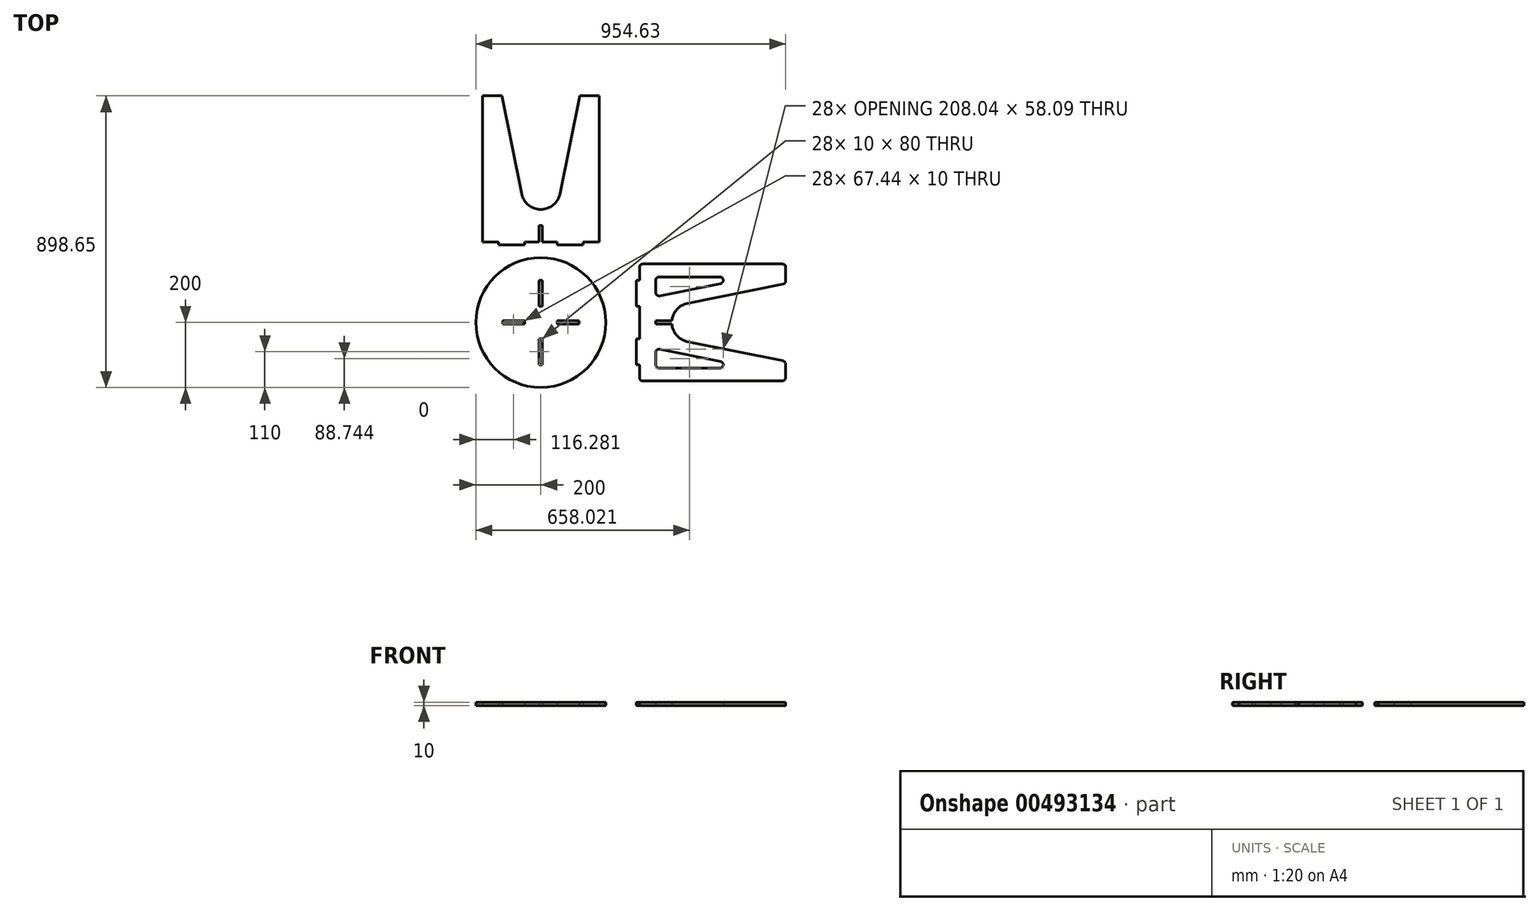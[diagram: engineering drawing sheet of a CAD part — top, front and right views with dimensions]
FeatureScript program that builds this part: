
annotation { "Feature Type Name" : "Feature", "Feature Type Description" : "" }
export const myFeature = defineFeature(function(context is Context, id is Id, definition is map)
    precondition{}
    {
        {
            var Q0;
            Q0=qCreatedBy(makeId("Top.planeOp"),FACE);
            var sketch = newSketch(context, id + "F0", { "sketchPlane" : qUnion([Q0])});
            skCircle(sketch, "E0", {"center": v(0, 0) * mm, "radius": 200 * mm});
            skLineSegment(sketch, "E1.bottom", {"start": v(-5, 130) * mm, "end": v(5, 130) * mm});
            skLineSegment(sketch, "E1.top", {"start": v(-5, 50) * mm, "end": v(5, 50) * mm});
            skLineSegment(sketch, "E1.left", {"start": v(-5, 130) * mm, "end": v(-5, 50) * mm});
            skLineSegment(sketch, "E1.right", {"start": v(5, 130) * mm, "end": v(5, 50) * mm});
            skLineSegment(sketch, "E2.MirrorCS", {"start": v(-5, -50) * mm, "end": v(5, -50) * mm});
            skLineSegment(sketch, "E3.MirrorCS", {"start": v(-5, -130) * mm, "end": v(5, -130) * mm});
            skLineSegment(sketch, "E4.MirrorCS", {"start": v(5, -130) * mm, "end": v(5, -50) * mm});
            skLineSegment(sketch, "E5.MirrorCS", {"start": v(-5, -130) * mm, "end": v(-5, -50) * mm});
            skLineSegment(sketch, "E6.MirrorCS", {"start": v(-117.44, -5) * mm, "end": v(-117.44, 5) * mm});
            skLineSegment(sketch, "E7.MirrorCS", {"start": v(-50, -5) * mm, "end": v(-50, 5) * mm});
            skLineSegment(sketch, "E8.MirrorCS", {"start": v(-50, 5) * mm, "end": v(-117.44, 5) * mm});
            skLineSegment(sketch, "E9.MirrorCS", {"start": v(-50, -5) * mm, "end": v(-117.44, -5) * mm});
            skLineSegment(sketch, "E10.MirrorCS", {"start": v(117.44, -5) * mm, "end": v(117.44, 5) * mm});
            skLineSegment(sketch, "E11.MirrorCS", {"start": v(50, 5) * mm, "end": v(117.44, 5) * mm});
            skLineSegment(sketch, "E12.MirrorCS", {"start": v(50, -5) * mm, "end": v(117.44, -5) * mm});
            skLineSegment(sketch, "E13.MirrorCS", {"start": v(50, -5) * mm, "end": v(50, 5) * mm});
            skLineSegment(sketch, "E14", {"start": v(-180, 248.65) * mm, "end": v(-130, 248.65) * mm});
            skLineSegment(sketch, "E15", {"start": v(180, 248.65) * mm, "end": v(180, 698.65) * mm});
            skLineSegment(sketch, "E16", {"start": v(180, 698.65) * mm, "end": v(120, 698.65) * mm});
            skLineSegment(sketch, "E17", {"start": v(120, 698.65) * mm, "end": v(58.8, 396.73) * mm});
            skLineSegment(sketch, "E18", {"start": v(130, 248.65) * mm, "end": v(130, 238.65) * mm});
            skLineSegment(sketch, "E19", {"start": v(130, 238.65) * mm, "end": v(50, 238.65) * mm});
            skLineSegment(sketch, "E20", {"start": v(50, 238.65) * mm, "end": v(50, 248.65) * mm});
            skLineSegment(sketch, "E21.trimOffspring", {"start": v(130, 248.65) * mm, "end": v(180, 248.65) * mm});
            skLineSegment(sketch, "E22.MirrorCS", {"start": v(-130, 248.65) * mm, "end": v(-130, 238.65) * mm});
            skLineSegment(sketch, "E23.MirrorCS", {"start": v(-50, 238.65) * mm, "end": v(-50, 248.65) * mm});
            skLineSegment(sketch, "E24.MirrorCS", {"start": v(-130, 238.65) * mm, "end": v(-50, 238.65) * mm});
            skLineSegment(sketch, "E25.MirrorCS", {"start": v(-180, 698.65) * mm, "end": v(-120, 698.65) * mm});
            skLineSegment(sketch, "E26.MirrorCS", {"start": v(-120, 698.65) * mm, "end": v(-58.8, 396.73) * mm});
            skLineSegment(sketch, "E27.trimOffspring", {"start": v(-50, 248.65) * mm, "end": v(-5, 248.65) * mm});
            skLineSegment(sketch, "E28", {"start": v(-180, 248.65) * mm, "end": v(-180, 698.65) * mm});
            skPoint(sketch, "E29.newPointA", {"position": v(-50, 353.3) * mm});
            skPoint(sketch, "E29.newPointB", {"position": v(50, 353.3) * mm});
            skArc(sketch, "E29.filletArc", {"start": v(-58.8, 396.73) * mm, "mid": v(0, 348.65) * mm, "end": v(58.8, 396.73) * mm});
            skLineSegment(sketch, "E30.bottom", {"start": v(-5, 298.65) * mm, "end": v(5, 298.65) * mm});
            skLineSegment(sketch, "E30.left", {"start": v(-5, 298.65) * mm, "end": v(-5, 248.65) * mm});
            skLineSegment(sketch, "E30.right", {"start": v(5, 298.65) * mm, "end": v(5, 248.65) * mm});
            skLineSegment(sketch, "E31.trimOffspring", {"start": v(5, 248.65) * mm, "end": v(50, 248.65) * mm});
            skLineSegment(sketch, "E32", {"start": v(304, 170.3) * mm, "end": v(304, 130.3) * mm});
            skLineSegment(sketch, "E33", {"start": v(314, -179.7) * mm, "end": v(744, -179.7) * mm});
            skLineSegment(sketch, "E34", {"start": v(754, -169.7) * mm, "end": v(754, -127.88) * mm});
            skLineSegment(sketch, "E35", {"start": v(745.98, -118.08) * mm, "end": v(451.7, -58.67) * mm});
            skLineSegment(sketch, "E36", {"start": v(304, -129.7) * mm, "end": v(294, -129.7) * mm});
            skLineSegment(sketch, "E37", {"start": v(294, -129.7) * mm, "end": v(294, -49.7) * mm});
            skLineSegment(sketch, "E38", {"start": v(294, -49.7) * mm, "end": v(304, -49.7) * mm});
            skLineSegment(sketch, "E39.trimOffspring", {"start": v(304, -129.7) * mm, "end": v(304, -169.7) * mm});
            skLineSegment(sketch, "E40.MirrorCS", {"start": v(304, 130.3) * mm, "end": v(294, 130.3) * mm});
            skLineSegment(sketch, "E41.MirrorCS", {"start": v(294, 50.3) * mm, "end": v(304, 50.3) * mm});
            skLineSegment(sketch, "E42.MirrorCS", {"start": v(294, 130.3) * mm, "end": v(294, 50.3) * mm});
            skLineSegment(sketch, "E43.MirrorCS", {"start": v(754.63, 170.3) * mm, "end": v(754.63, 128.48) * mm});
            skLineSegment(sketch, "E44.MirrorCS", {"start": v(746.61, 118.68) * mm, "end": v(451.67, 58.95) * mm});
            skLineSegment(sketch, "E45", {"start": v(314, 180.3) * mm, "end": v(744.63, 180.3) * mm});
            skPoint(sketch, "E46.newPointA", {"position": v(409.36, 50.38) * mm});
            skPoint(sketch, "E46.newPointB", {"position": v(407.26, -49.7) * mm});
            skArc(sketch, "E46.filletArc", {"start": v(451.67, 58.95) * mm, "mid": v(418.75, 40.03) * mm, "end": v(403.78, 5.14) * mm});
            skLineSegment(sketch, "E47.bottom", {"start": v(-262.6, 711.4) * mm, "end": v(-252.6, 711.4) * mm});
            skLineSegment(sketch, "E48", {"start": v(353.78, 5.12) * mm, "end": v(353.8, -4.88) * mm});
            skLineSegment(sketch, "E49.MirrorCS", {"start": v(353.78, 5.12) * mm, "end": v(403.78, 5.14) * mm});
            skLineSegment(sketch, "E50.MirrorCS", {"start": v(353.8, -4.88) * mm, "end": v(403.79, -4.86) * mm});
            skArc(sketch, "E51.trimOffspring", {"start": v(403.79, -4.86) * mm, "mid": v(418.77, -39.76) * mm, "end": v(451.7, -58.67) * mm});
            skLineSegment(sketch, "E52", {"start": v(304, 50.3) * mm, "end": v(304, -49.7) * mm});
            skLineSegment(sketch, "E53.0", {"start": v(364, 140.3) * mm, "end": v(552.1, 140.3) * mm});
            skLineSegment(sketch, "E54.0", {"start": v(354, 130.3) * mm, "end": v(354, 92.2) * mm});
            skPoint(sketch, "E55.visualSharp", {"position": v(354, 79.98) * mm});
            skArc(sketch, "E55.filletArc", {"start": v(354, 92.2) * mm, "mid": v(357.67, 84.47) * mm, "end": v(365.98, 82.4) * mm});
            skPoint(sketch, "E56.visualSharp", {"position": v(354, 140.3) * mm});
            skArc(sketch, "E56.filletArc", {"start": v(364, 140.3) * mm, "mid": v(356.93, 137.37) * mm, "end": v(354, 130.3) * mm});
            skPoint(sketch, "E57.visualSharp", {"position": v(651.86, 140.3) * mm});
            skArc(sketch, "E57.filletArc", {"start": v(554.08, 120.5) * mm, "mid": v(562.04, 131.3) * mm, "end": v(552.1, 140.3) * mm});
            skPoint(sketch, "E58.visualSharp", {"position": v(304, 180.3) * mm});
            skArc(sketch, "E58.filletArc", {"start": v(314, 180.3) * mm, "mid": v(306.93, 177.37) * mm, "end": v(304, 170.3) * mm});
            skPoint(sketch, "E59.visualSharp", {"position": v(754.63, 180.3) * mm});
            skArc(sketch, "E59.filletArc", {"start": v(754.63, 170.3) * mm, "mid": v(751.7, 177.37) * mm, "end": v(744.63, 180.3) * mm});
            skPoint(sketch, "E60.visualSharp", {"position": v(754.63, 120.3) * mm});
            skArc(sketch, "E60.filletArc", {"start": v(746.61, 118.68) * mm, "mid": v(752.37, 122.15) * mm, "end": v(754.63, 128.48) * mm});
            skPoint(sketch, "E61.visualSharp", {"position": v(304, -179.7) * mm});
            skArc(sketch, "E61.filletArc", {"start": v(304, -169.7) * mm, "mid": v(306.93, -176.77) * mm, "end": v(314, -179.7) * mm});
            skPoint(sketch, "E62.visualSharp", {"position": v(754, -119.7) * mm});
            skArc(sketch, "E62.filletArc", {"start": v(754, -127.88) * mm, "mid": v(751.74, -121.55) * mm, "end": v(745.98, -118.08) * mm});
            skPoint(sketch, "E63.visualSharp", {"position": v(754, -179.7) * mm});
            skArc(sketch, "E63.filletArc", {"start": v(744, -179.7) * mm, "mid": v(751.07, -176.77) * mm, "end": v(754, -169.7) * mm});
            skLineSegment(sketch, "E64", {"start": v(365.98, 82.4) * mm, "end": v(554.08, 120.5) * mm});
            skArc(sketch, "E65.MirrorCS", {"start": v(354, -92.2) * mm, "mid": v(357.67, -84.47) * mm, "end": v(365.98, -82.4) * mm});
            skArc(sketch, "E66.MirrorCS", {"start": v(364, -140.3) * mm, "mid": v(356.93, -137.37) * mm, "end": v(354, -130.3) * mm});
            skLineSegment(sketch, "E67.MirrorCS", {"start": v(364, -140.3) * mm, "end": v(552.1, -140.3) * mm});
            skPoint(sketch, "E68.MirrorP", {"position": v(354, -140.3) * mm});
            skLineSegment(sketch, "E69.MirrorCS", {"start": v(365.98, -82.4) * mm, "end": v(554.08, -120.5) * mm});
            skLineSegment(sketch, "E70.MirrorCS", {"start": v(354, -130.3) * mm, "end": v(354, -92.2) * mm});
            skArc(sketch, "E71.MirrorCS", {"start": v(554.08, -120.5) * mm, "mid": v(562.04, -131.3) * mm, "end": v(552.1, -140.3) * mm});
            skSolve(sketch);
        }
        {
            var Q0;
            Q0=qSketchRegion(id+"F0",true);
            extrude(context, id + "F1", {"entities" : qUnion([Q0]), "depth" : 10 * mm});
        }
    });
